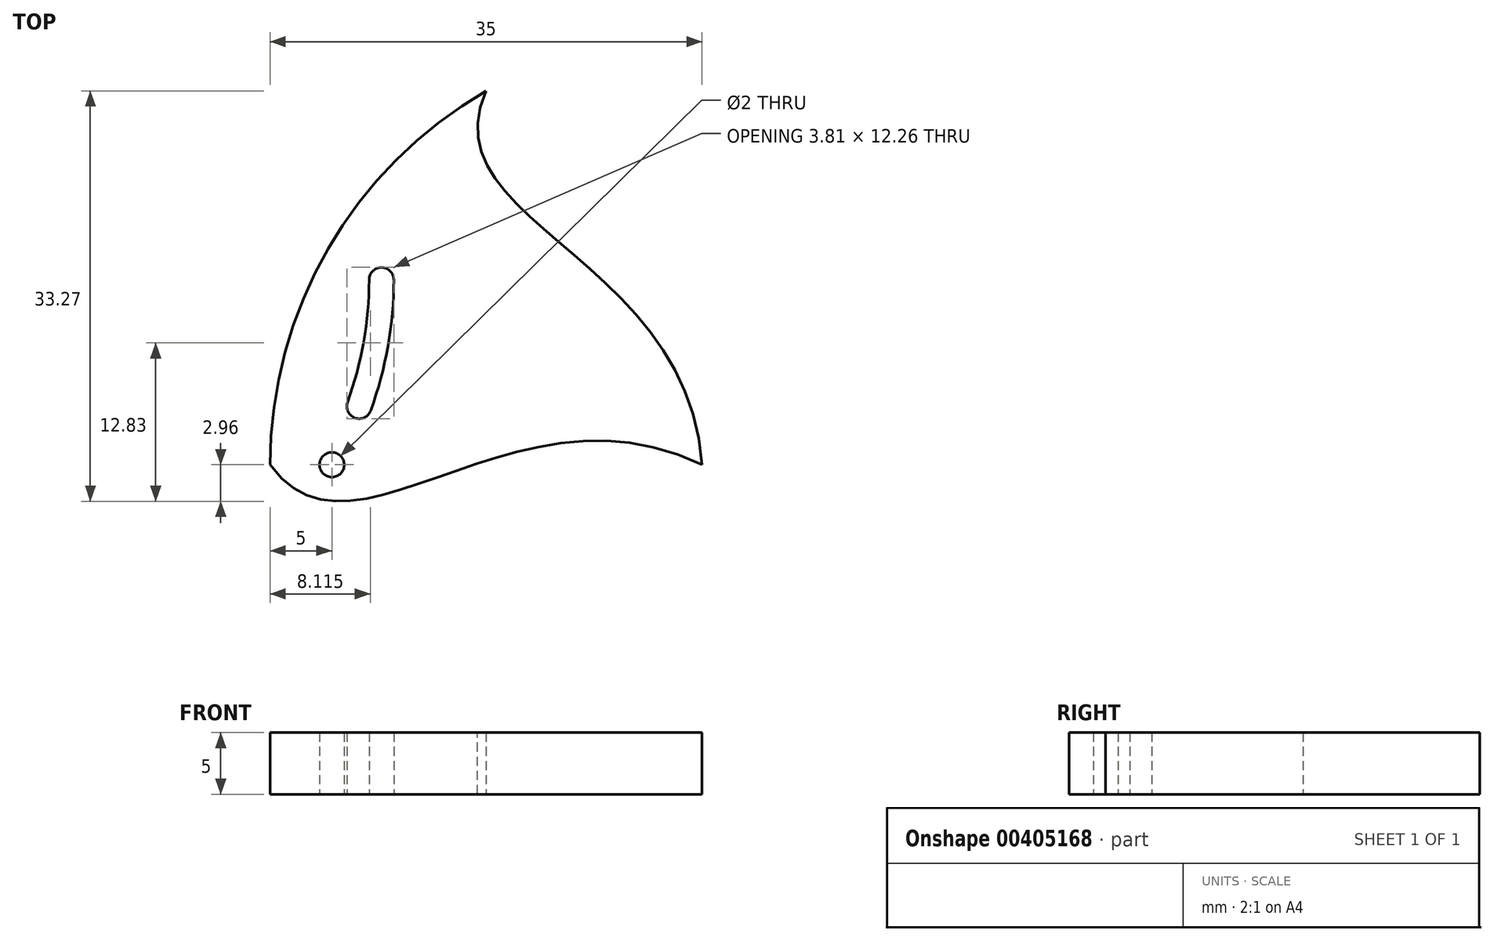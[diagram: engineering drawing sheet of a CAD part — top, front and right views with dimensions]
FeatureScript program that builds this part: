
annotation { "Feature Type Name" : "Feature", "Feature Type Description" : "" }
export const myFeature = defineFeature(function(context is Context, id is Id, definition is map)
    precondition{}
    {
        {
            var Q0;
            Q0=qCreatedBy(makeId("Top.planeOp"),FACE);
            var sketch = newSketch(context, id + "F0", { "sketchPlane" : qUnion([Q0])});
            skCircle(sketch, "E0", {"center": v(0, 0) * mm, "radius": 1 * mm});
            skLineSegment(sketch, "E1", {"start": v(-5, 0) * mm, "end": v(5, 0) * mm, "construction": true});
            skLineSegment(sketch, "E2", {"start": v(-5, 0) * mm, "end": v(30, 0) * mm, "construction": true});
            skLineSegment(sketch, "E3", {"start": v(30, 0) * mm, "end": v(12.5, 30.31) * mm, "construction": true});
            skLineSegment(sketch, "E4", {"start": v(12.5, 30.31) * mm, "end": v(-5, 0) * mm, "construction": true});
            skArc(sketch, "E5", {"start": v(12.5, 30.31) * mm, "mid": v(-0.31, 17.5) * mm, "end": v(-5, 0) * mm});
            skLineSegment(sketch, "E6", {"start": v(0, 0) * mm, "end": v(0, -5) * mm, "construction": true});
            skFitSpline(sketch, "E7", {"points": [v(-5, 0) * mm, v(30, 0) * mm], "startDerivative": vector(20.44, -28.34) * mm, "endDerivative": vector(46.09, -22.26) * mm});
            skFitSpline(sketch, "E8", {"points": [v(12.5, 30.31) * mm, v(30, 0) * mm], "startDerivative": vector(-14.32, -31.88) * mm, "endDerivative": vector(3.77, -51.04) * mm});
            skArc(sketch, "E9", {"start": v(0, 0) * mm, "mid": v(1.2, 2.32) * mm, "end": v(2.21, 4.74) * mm, "construction": true});
            skArc(sketch, "E10", {"start": v(1.27, 5.08) * mm, "mid": v(1.87, 3.8) * mm, "end": v(3.15, 4.4) * mm});
            skArc(sketch, "E11.0", {"start": v(3.15, 4.4) * mm, "mid": v(4.55, 9.62) * mm, "end": v(5.02, 15) * mm});
            skArc(sketch, "E12.0", {"start": v(1.27, 5.08) * mm, "mid": v(2.58, 9.96) * mm, "end": v(3.02, 15) * mm});
            skArc(sketch, "E13", {"start": v(5.02, 15) * mm, "mid": v(4.02, 16) * mm, "end": v(3.02, 15) * mm});
            skArc(sketch, "E14", {"start": v(15, 25.98) * mm, "mid": v(3.31, 13.7) * mm, "end": v(0.14, -2.94) * mm, "construction": true});
            skSolve(sketch);
        }
        {
            var Q0;
            Q0=makeQuery(id+"F0.imprint","IMPRINT",FACE,{"disambiguationData":[TD([[makeQuery(id+"F0.imprint","IMPRINT",EDGE,{"derivedFrom":sQuery(id+"F0.wireOp",EDGE,"E0")}),-1.0]])]});
            extrude(context, id + "F1", {"entities" : qUnion([Q0]), "depth" : 5 * mm});
        }
    });
